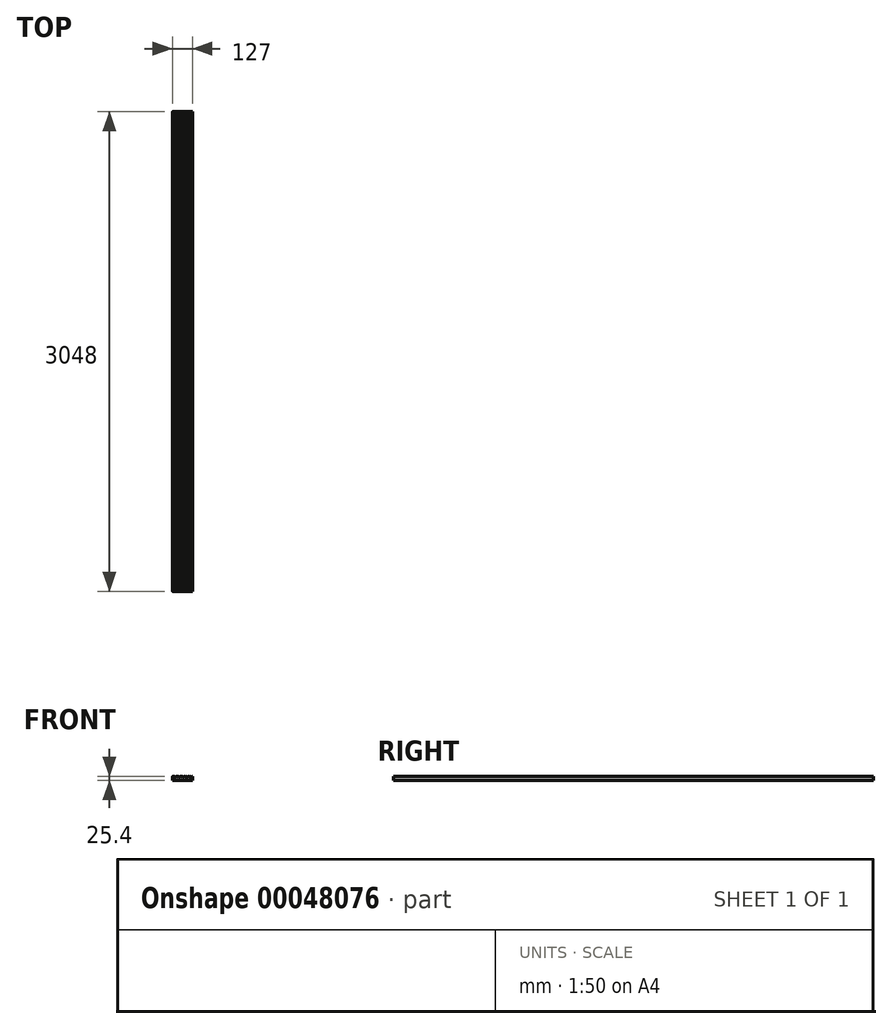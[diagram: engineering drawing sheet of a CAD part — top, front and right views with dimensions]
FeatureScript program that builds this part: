
annotation { "Feature Type Name" : "Feature", "Feature Type Description" : "" }
export const myFeature = defineFeature(function(context is Context, id is Id, definition is map)
    precondition{}
    {
        {
            var Q0;
            Q0=qCreatedBy(makeId("Front.planeOp"),FACE);
            var sketch = newSketch(context, id + "F0", { "sketchPlane" : qUnion([Q0])});
            skLineSegment(sketch, "E0.bottom", {"start": v(-63.25, 12.7) * mm, "end": v(-60.58, 12.7) * mm});
            skLineSegment(sketch, "E0.top", {"start": v(-63.5, -12.7) * mm, "end": v(63.5, -12.7) * mm});
            skLineSegment(sketch, "E0.left", {"start": v(-63.5, 12.45) * mm, "end": v(-63.5, -12.7) * mm});
            skLineSegment(sketch, "E0.right", {"start": v(63.5, 12.7) * mm, "end": v(63.5, -12.7) * mm});
            skLineSegment(sketch, "E1", {"start": v(-60.33, 10.41) * mm, "end": v(-60.33, 12.45) * mm});
            skLineSegment(sketch, "E2", {"start": v(-60.07, 10.16) * mm, "end": v(-54.23, 10.16) * mm});
            skLineSegment(sketch, "E3", {"start": v(-53.98, 10.41) * mm, "end": v(-53.98, 12.45) * mm});
            skLineSegment(sketch, "E4.trimOffspring", {"start": v(-53.72, 12.7) * mm, "end": v(63.5, 12.7) * mm});
            skLineSegment(sketch, "E5.1.0.0", {"start": v(-41.27, 10.16) * mm, "end": v(-41.27, 12.7) * mm});
            skLineSegment(sketch, "E5.1.0.1", {"start": v(-47.62, 10.16) * mm, "end": v(-41.27, 10.16) * mm});
            skLineSegment(sketch, "E5.1.0.2", {"start": v(-47.62, 10.16) * mm, "end": v(-47.62, 12.7) * mm});
            skLineSegment(sketch, "E5.2.0.0", {"start": v(-28.57, 10.16) * mm, "end": v(-28.57, 12.7) * mm});
            skLineSegment(sketch, "E5.2.0.1", {"start": v(-34.92, 10.16) * mm, "end": v(-28.57, 10.16) * mm});
            skLineSegment(sketch, "E5.2.0.2", {"start": v(-34.92, 10.16) * mm, "end": v(-34.92, 12.7) * mm});
            skLineSegment(sketch, "E5.3.0.0", {"start": v(-15.87, 10.16) * mm, "end": v(-15.87, 12.7) * mm});
            skLineSegment(sketch, "E5.3.0.1", {"start": v(-22.22, 10.16) * mm, "end": v(-15.87, 10.16) * mm});
            skLineSegment(sketch, "E5.3.0.2", {"start": v(-22.22, 10.16) * mm, "end": v(-22.22, 12.7) * mm});
            skLineSegment(sketch, "E5.4.0.0", {"start": v(-3.17, 10.16) * mm, "end": v(-3.17, 12.7) * mm});
            skLineSegment(sketch, "E5.4.0.1", {"start": v(-9.52, 10.16) * mm, "end": v(-3.17, 10.16) * mm});
            skLineSegment(sketch, "E5.4.0.2", {"start": v(-9.52, 10.16) * mm, "end": v(-9.52, 12.7) * mm});
            skLineSegment(sketch, "E5.5.0.0", {"start": v(9.53, 10.16) * mm, "end": v(9.53, 12.7) * mm});
            skLineSegment(sketch, "E5.5.0.1", {"start": v(3.18, 10.16) * mm, "end": v(9.53, 10.16) * mm});
            skLineSegment(sketch, "E5.5.0.2", {"start": v(3.18, 10.16) * mm, "end": v(3.18, 12.7) * mm});
            skLineSegment(sketch, "E5.6.0.0", {"start": v(22.23, 10.16) * mm, "end": v(22.23, 12.7) * mm});
            skLineSegment(sketch, "E5.6.0.1", {"start": v(15.88, 10.16) * mm, "end": v(22.23, 10.16) * mm});
            skLineSegment(sketch, "E5.6.0.2", {"start": v(15.88, 10.16) * mm, "end": v(15.88, 12.7) * mm});
            skLineSegment(sketch, "E5.7.0.0", {"start": v(34.93, 10.16) * mm, "end": v(34.93, 12.7) * mm});
            skLineSegment(sketch, "E5.7.0.1", {"start": v(28.58, 10.16) * mm, "end": v(34.93, 10.16) * mm});
            skLineSegment(sketch, "E5.7.0.2", {"start": v(28.58, 10.16) * mm, "end": v(28.58, 12.7) * mm});
            skLineSegment(sketch, "E5.8.0.0", {"start": v(47.63, 10.16) * mm, "end": v(47.63, 12.7) * mm});
            skLineSegment(sketch, "E5.8.0.1", {"start": v(41.28, 10.16) * mm, "end": v(47.63, 10.16) * mm});
            skLineSegment(sketch, "E5.8.0.2", {"start": v(41.28, 10.16) * mm, "end": v(41.28, 12.7) * mm});
            skLineSegment(sketch, "E5.9.0.0", {"start": v(60.33, 10.16) * mm, "end": v(60.33, 12.7) * mm});
            skLineSegment(sketch, "E5.9.0.1", {"start": v(53.98, 10.16) * mm, "end": v(60.33, 10.16) * mm});
            skLineSegment(sketch, "E5.9.0.2", {"start": v(53.98, 10.16) * mm, "end": v(53.98, 12.7) * mm});
            skLineSegment(sketch, "E5.direction1", {"start": v(-53.98, 10.16) * mm, "end": v(-41.27, 10.16) * mm, "construction": true});
            skPoint(sketch, "E6.visualSharp", {"position": v(-60.33, 12.7) * mm});
            skArc(sketch, "E6.filletArc", {"start": v(-60.32, 12.45) * mm, "mid": v(-60.4, 12.63) * mm, "end": v(-60.58, 12.7) * mm});
            skPoint(sketch, "E7.visualSharp", {"position": v(-60.33, 10.16) * mm});
            skArc(sketch, "E7.filletArc", {"start": v(-60.33, 10.41) * mm, "mid": v(-60.25, 10.23) * mm, "end": v(-60.07, 10.16) * mm});
            skPoint(sketch, "E8.visualSharp", {"position": v(-53.98, 10.16) * mm});
            skArc(sketch, "E8.filletArc", {"start": v(-54.23, 10.16) * mm, "mid": v(-54.05, 10.23) * mm, "end": v(-53.98, 10.41) * mm});
            skPoint(sketch, "E9.visualSharp", {"position": v(-53.98, 12.7) * mm});
            skArc(sketch, "E9.filletArc", {"start": v(-53.72, 12.7) * mm, "mid": v(-53.9, 12.63) * mm, "end": v(-53.98, 12.45) * mm});
            skPoint(sketch, "E10.visualSharp", {"position": v(-63.5, 12.7) * mm});
            skArc(sketch, "E10.filletArc", {"start": v(-63.25, 12.7) * mm, "mid": v(-63.43, 12.63) * mm, "end": v(-63.5, 12.45) * mm});
            skSolve(sketch);
        }
        {
            var Q0;
            Q0=makeQuery(id+"F0.imprint","IMPRINT",FACE,{"disambiguationData":[TD([[makeQuery(id+"F0.imprint","IMPRINT",EDGE,{"derivedFrom":sQuery(id+"F0.wireOp",EDGE,"E0.bottom")}),-1.0]])]});
            extrude(context, id + "F1", {"entities" : qUnion([Q0]), "endBound" : BoundingType.SYMMETRIC, "depth" : 3048 * mm});
        }
    });
